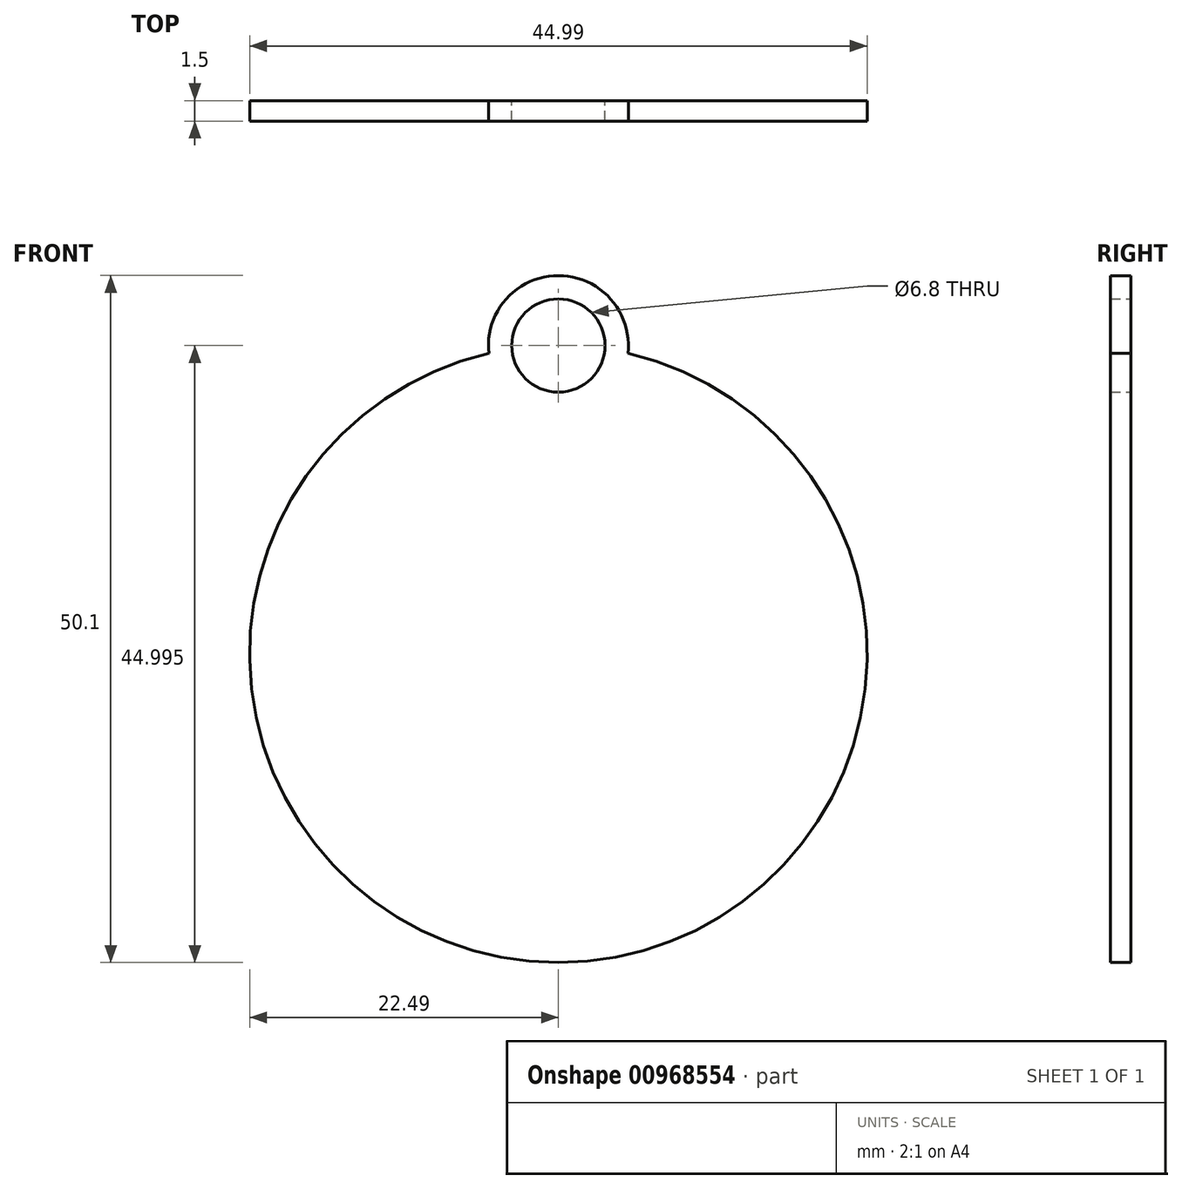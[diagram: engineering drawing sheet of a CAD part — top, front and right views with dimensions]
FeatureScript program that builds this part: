
annotation { "Feature Type Name" : "Feature", "Feature Type Description" : "" }
export const myFeature = defineFeature(function(context is Context, id is Id, definition is map)
    precondition{}
    {
        {
            var Q0;
            Q0=qCreatedBy(makeId("Front.planeOp"),FACE);
            var sketch = newSketch(context, id + "F0", { "sketchPlane" : qUnion([Q0])});
            skArc(sketch, "E0", {"start": v(-5.07, 21.92) * mm, "mid": v(0, -22.5) * mm, "end": v(5.07, 21.92) * mm});
            skCircle(sketch, "E1", {"center": v(0, 22.5) * mm, "radius": 5.1 * mm});
            skCircle(sketch, "E2", {"center": v(0, 22.5) * mm, "radius": 3.4 * mm});
            skSolve(sketch);
        }
        {
            var Q0;
            {var subQ0=sQuery(id+"F0.wireOp",EDGE,"E1");var subQ1=sQuery(id+"F0.wireOp",EDGE,"E0");var subQ2=makeQuery(id+"F0.imprint","INTERSECT",VERTEX,{"disambiguationData":[OD(0.0)],"derivedFrom":[subQ1,subQ0]});Q0=makeQuery(id+"F0.imprint","IMPRINT",FACE,{"disambiguationData":[TD([[makeQuery(id+"F0.imprint","IMPRINT",EDGE,{"disambiguationData":[TD([[subQ2,-1.0]])],"derivedFrom":subQ0}),1.0]])]});}
            var Q1;
            {var subQ0=sQuery(id+"F0.wireOp",EDGE,"E0");Q1=makeQuery(id+"F0.imprint","IMPRINT",FACE,{"disambiguationData":[TD([[makeQuery(id+"F0.imprint","IMPRINT",EDGE,{"derivedFrom":subQ0}),1.0]])]});}
            extrude(context, id + "F1", {"entities" : qUnion([Q0, Q1]), "depth" : 1.5 * mm, "offsetDistance" : 25 * mm});
        }
    });
